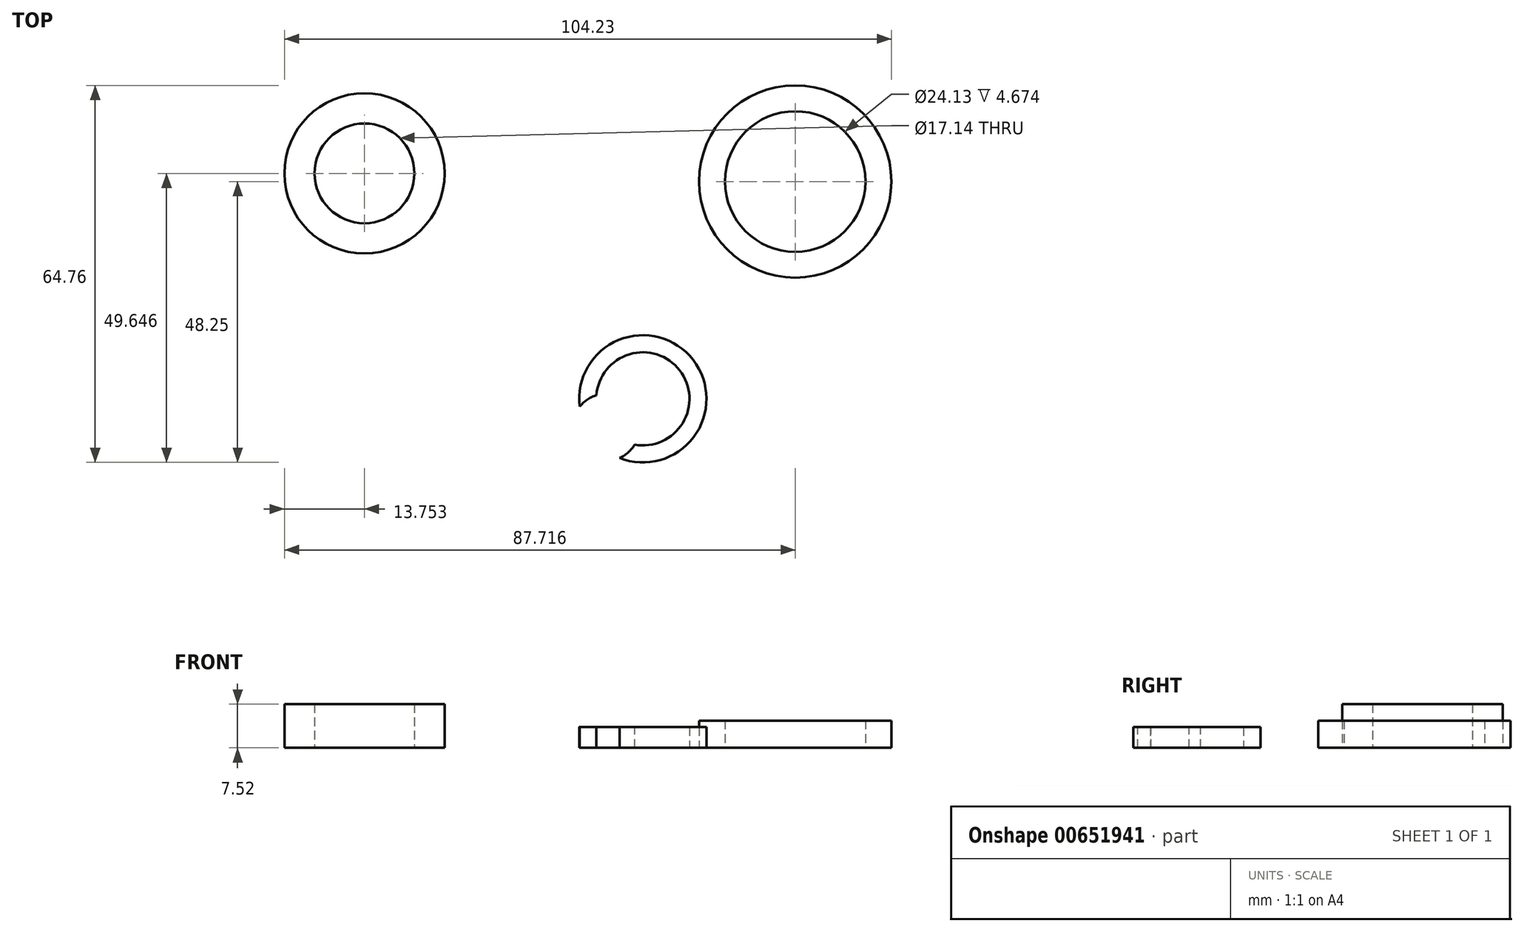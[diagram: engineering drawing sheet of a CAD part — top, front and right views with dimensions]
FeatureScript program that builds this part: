
annotation { "Feature Type Name" : "Feature", "Feature Type Description" : "" }
export const myFeature = defineFeature(function(context is Context, id is Id, definition is map)
    precondition{}
    {
        {
            var Q0;
            Q0=qCreatedBy(makeId("Top.planeOp"),FACE);
            var sketch = newSketch(context, id + "F0", { "sketchPlane" : qUnion([Q0])});
            skCircle(sketch, "E0", {"center": v(0, 0) * mm, "radius": 8 * mm});
            skCircle(sketch, "E1", {"center": v(0, 0) * mm, "radius": 10.92 * mm});
            skSolve(sketch);
        }
        {
            var Q0;
            Q0 = qSketchRegion(id + "F0", true);
            extrude(context, id + "F1", {"entities" : qUnion([Q0]), "depth" : 3.56 * mm, "offsetDistance" : 25.4 * mm});
        }
        {
            var Q0;
            Q0=makeQuery(id+"F1.opExtrude","CAP_FACE",FACE,{"disambiguationData":[OSD([sQuery(id+"F0.wireOp",EDGE,"E0"),sQuery(id+"F0.wireOp",EDGE,"E1")])],"isStart":false});
            var sketch = newSketch(context, id + "F2", { "sketchPlane" : qUnion([Q0])});
            skCircle(sketch, "E2", {"center": v(-6.33, -4.9) * mm, "radius": 5.75 * mm});
            skSolve(sketch);
        }
        {
            var Q0;
            Q0 = qSketchRegion(id + "F2", true);
            extrude(context, id + "F3", {"entities" : qUnion([Q0]), "operationType" : NewBodyOperationType.REMOVE, "oppositeDirection" : true, "depth" : 4.7 * mm, "offsetDistance" : 25.4 * mm});
        }
        {
            var Q0;
            Q0=qCreatedBy(makeId("Top.planeOp"),FACE);
            var sketch = newSketch(context, id + "F4", { "sketchPlane" : qUnion([Q0])});
            skCircle(sketch, "E3", {"center": v(-47.8, 38.73) * mm, "radius": 8.57 * mm});
            skCircle(sketch, "E4", {"center": v(-47.8, 38.73) * mm, "radius": 13.75 * mm});
            skSolve(sketch);
        }
        {
            var Q0;
            Q0 = qSketchRegion(id + "F4", true);
            extrude(context, id + "F5", {"entities" : qUnion([Q0]), "depth" : 7.52 * mm, "offsetDistance" : 25.4 * mm});
        }
        {
            var Q0;
            Q0=qCreatedBy(makeId("Top.planeOp"),FACE);
            var sketch = newSketch(context, id + "F6", { "sketchPlane" : qUnion([Q0])});
            skCircle(sketch, "E5", {"center": v(26.17, 37.33) * mm, "radius": 12.07 * mm});
            skCircle(sketch, "E6", {"center": v(26.17, 37.33) * mm, "radius": 16.51 * mm});
            skSolve(sketch);
        }
        {
            var Q0;
            Q0 = qSketchRegion(id + "F6", true);
            extrude(context, id + "F7", {"entities" : qUnion([Q0]), "depth" : 4.67 * mm, "offsetDistance" : 25.4 * mm});
        }
    });
